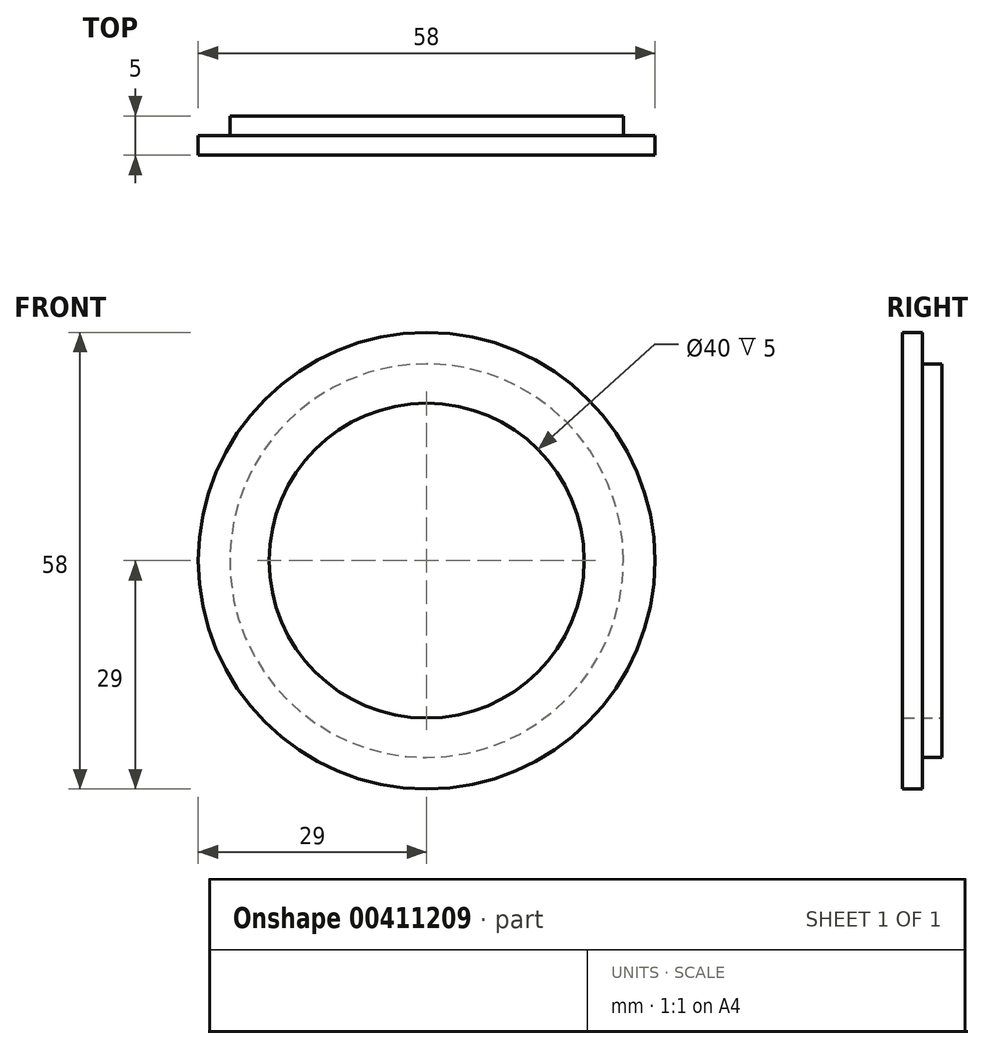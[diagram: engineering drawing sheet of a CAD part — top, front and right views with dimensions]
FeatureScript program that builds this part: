
annotation { "Feature Type Name" : "Feature", "Feature Type Description" : "" }
export const myFeature = defineFeature(function(context is Context, id is Id, definition is map)
    precondition{}
    {
        {
            var Q0;
            Q0=qCreatedBy(makeId("Front.planeOp"),FACE);
            var sketch = newSketch(context, id + "F0", { "sketchPlane" : qUnion([Q0])});
            skCircle(sketch, "E0", {"center": v(0, 0) * mm, "radius": 25 * mm});
            skCircle(sketch, "E1.0", {"center": v(0, 0) * mm, "radius": 29 * mm});
            skCircle(sketch, "E2.0", {"center": v(0, 0) * mm, "radius": 23 * mm});
            skCircle(sketch, "E3.0", {"center": v(0, 0) * mm, "radius": 20 * mm});
            skSolve(sketch);
        }
        {
            var Q0;
            Q0=makeQuery(id+"F0.imprint","IMPRINT",FACE,{"disambiguationData":[TD([[makeQuery(id+"F0.imprint","IMPRINT",EDGE,{"derivedFrom":sQuery(id+"F0.wireOp",EDGE,"E0")}),-1.0]])]});
            var Q1;
            Q1=makeQuery(id+"F0.imprint","IMPRINT",FACE,{"disambiguationData":[TD([[makeQuery(id+"F0.imprint","IMPRINT",EDGE,{"derivedFrom":sQuery(id+"F0.wireOp",EDGE,"E2.0")}),1.0]])]});
            var Q2;
            Q2=makeQuery(id+"F0.imprint","IMPRINT",FACE,{"disambiguationData":[TD([[makeQuery(id+"F0.imprint","IMPRINT",EDGE,{"derivedFrom":sQuery(id+"F0.wireOp",EDGE,"E0")}),1.0]])]});
            extrude(context, id + "F1", {"entities" : qUnion([Q0, Q1, Q2]), "depth" : 2.5 * mm, "offsetDistance" : 25 * mm});
        }
        {
            var Q0;
            Q0=makeQuery(id+"F0.imprint","IMPRINT",FACE,{"disambiguationData":[TD([[makeQuery(id+"F0.imprint","IMPRINT",EDGE,{"derivedFrom":sQuery(id+"F0.wireOp",EDGE,"E2.0")}),1.0]])]});
            var Q1;
            Q1=makeQuery(id+"F0.imprint","IMPRINT",FACE,{"disambiguationData":[TD([[makeQuery(id+"F0.imprint","IMPRINT",EDGE,{"derivedFrom":sQuery(id+"F0.wireOp",EDGE,"E0")}),1.0]])]});
            extrude(context, id + "F2", {"entities" : qUnion([Q0, Q1]), "operationType" : NewBodyOperationType.ADD, "oppositeDirection" : true, "depth" : 5 * mm, "offsetDistance" : 25 * mm, "symmetric" : true});
        }
        {
            var Q0;
            Q0=sQuery(id+"F0.wireOp",EDGE,"E2.0");
            var Q1;
            Q1=sQuery(id+"F0.wireOp",EDGE,"E0");
            extrude(context, id + "F3", {"bodyType" : ToolBodyType.SURFACE, "surfaceEntities" : qUnion([Q0, Q1]), "depth" : 5 * mm, "offsetDistance" : 25 * mm, "symmetric" : true});
        }
    });
